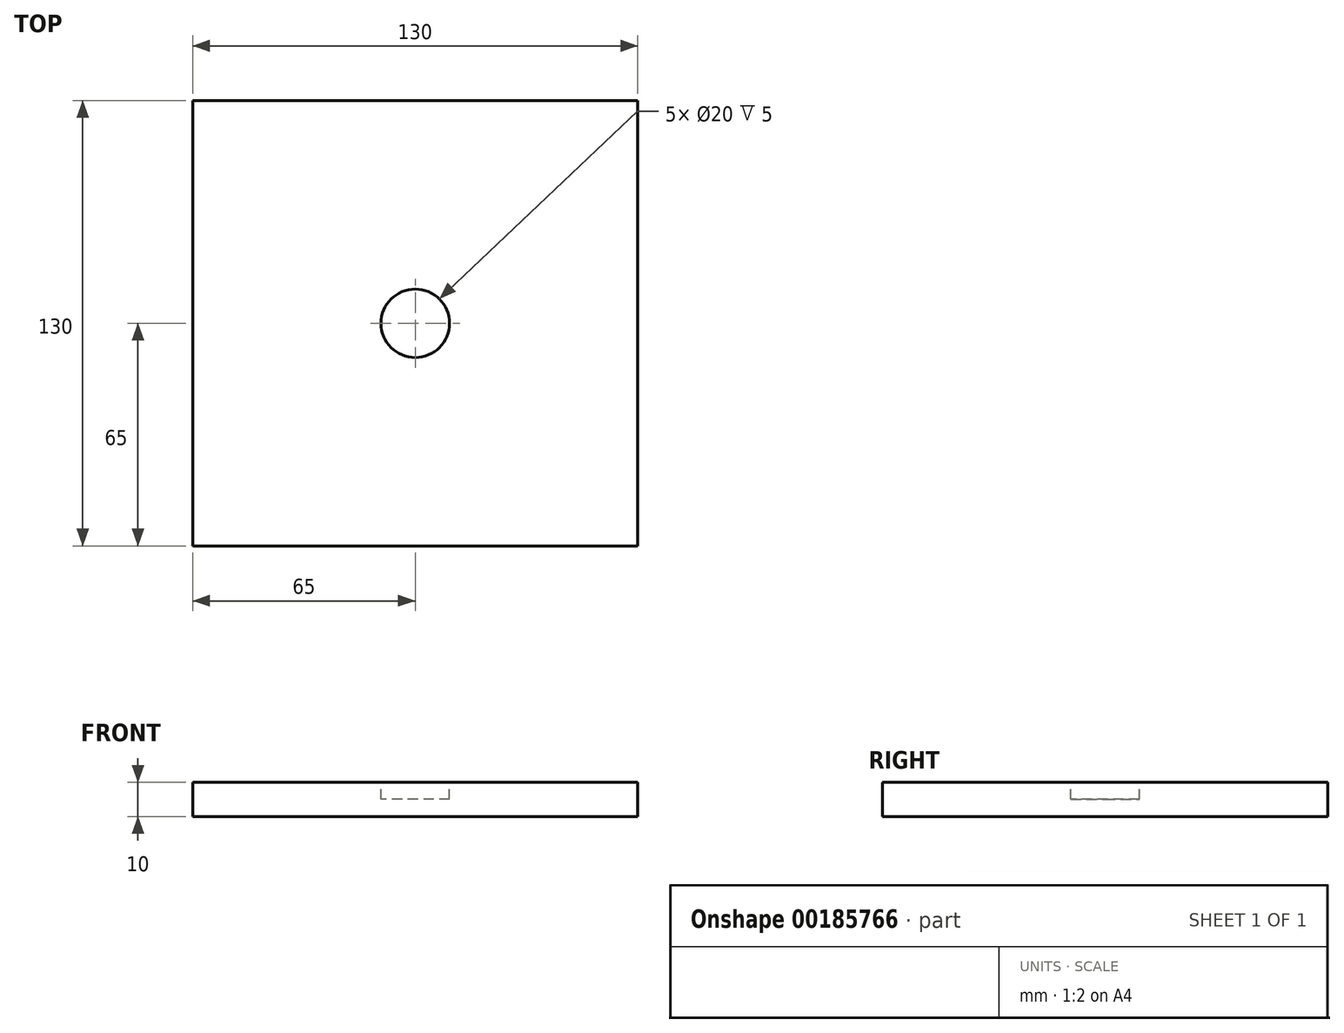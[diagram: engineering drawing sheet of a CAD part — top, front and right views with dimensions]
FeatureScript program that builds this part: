
annotation { "Feature Type Name" : "Feature", "Feature Type Description" : "" }
export const myFeature = defineFeature(function(context is Context, id is Id, definition is map)
    precondition{}
    {
        {
            var Q0;
            Q0=qCreatedBy(makeId("Top.planeOp"),FACE);
            var sketch = newSketch(context, id + "F0", { "sketchPlane" : qUnion([Q0])});
            skLineSegment(sketch, "E0.bottom", {"start": v(65, 65) * mm, "end": v(-65, 65) * mm});
            skLineSegment(sketch, "E0.top", {"start": v(65, -65) * mm, "end": v(-65, -65) * mm});
            skLineSegment(sketch, "E0.left", {"start": v(65, 65) * mm, "end": v(65, -65) * mm});
            skLineSegment(sketch, "E0.right", {"start": v(-65, 65) * mm, "end": v(-65, -65) * mm});
            skPoint(sketch, "E0.middle", {"position": v(0, 0) * mm});
            skSolve(sketch);
        }
        {
            var Q0;
            Q0 = qSketchRegion(id + "F0", true);
            extrude(context, id + "F1", {"entities" : qUnion([Q0]), "depth" : 10 * mm});
        }
        {
            var Q0;
            Q0=makeQuery(id+"F1.opExtrude","CAP_FACE",FACE,{"disambiguationData":[OSD([sQuery(id+"F0.wireOp",EDGE,"E0.bottom"),sQuery(id+"F0.wireOp",EDGE,"E0.top"),sQuery(id+"F0.wireOp",EDGE,"E0.left"),sQuery(id+"F0.wireOp",EDGE,"E0.right")])],"isStart":false});
            var sketch = newSketch(context, id + "F2", { "sketchPlane" : qUnion([Q0])});
            skCircle(sketch, "E1", {"center": v(0, 0) * mm, "radius": 10 * mm});
            skCircle(sketch, "E2.1.0.0", {"center": v(25, 0) * mm, "radius": 10 * mm});
            skCircle(sketch, "E2.2.0.0", {"center": v(50, 0) * mm, "radius": 10 * mm});
            skLineSegment(sketch, "E2.direction1", {"start": v(0, 0) * mm, "end": v(25, 0) * mm, "construction": true});
            skSolve(sketch);
        }
        {
            var Q0;
            Q0=makeQuery(id+"F2.imprint","IMPRINT",FACE,{"disambiguationData":[TD([[makeQuery(id+"F2.imprint","IMPRINT",EDGE,{"derivedFrom":sQuery(id+"F2.wireOp",EDGE,"E1")}),1.0]])]});
            extrude(context, id + "F3", {"entities" : qUnion([Q0]), "operationType" : NewBodyOperationType.REMOVE, "oppositeDirection" : true, "depth" : 5 * mm});
        }
    });
